# Revit family: MW_Nevada luchtverwarmer
name_source: partatom
category: Mechanical Equipment
units: mm (PartAtom-declared; Revit-internal decimal feet)

## family parameters
Always vertical = Yes
Cut with Voids When Loaded = No
OmniClass Number = 23.75.00.00
OmniClass Title = Climate Control (HVAC)
Part Type = Normal
Room Calculation Point = No
Round Connector Dimension = Use Diameter
Shared = No
Work Plane-Based = No

## types (9) — shared parameters
Manufacturer = Masterwatt B.V.
Materiaal 1 = Coating wit
URL = https://masterwatt.nl
Voltage = 400 V
zero-valued in all types: Default Elevation

## per-type parameters (varying)
| type | Art. No. | Beugel | Breedte | Product type | Watt |
| Nevada 1E 4,5 | 700 100 045 | Nevada_arm : 1E | 530 mm  [stored 1.73885 ft] | Nevada Luchtverwarmer : Nevada 1E 4,5 | 4500 VA |
| Nevada 2E 10,0 | 700 100 100 | Nevada_arm : 2E | 680 mm  [stored 2.23097 ft] | Nevada Luchtverwarmer : Nevada 2E 10,0 | 10000 VA |
| Nevada 1E 6,0 | 700 100 060 | Nevada_arm : 1E | 530 mm  [stored 1.73885 ft] | Nevada Luchtverwarmer : Nevada 1E 4,5 | 6000 VA |
| Nevada 1E 7,5 | 700 100 075 | Nevada_arm : 1E | 530 mm  [stored 1.73885 ft] | Nevada Luchtverwarmer : Nevada 1E 4,5 | 7500 VA |
| Nevada 1E 9,0 | 700 100 090 | Nevada_arm : 1E | 530 mm  [stored 1.73885 ft] | Nevada Luchtverwarmer : Nevada 1E 4,5 | 9000 VA |
| Nevada 2E 12,5 | 700 100 125 | Nevada_arm : 2E | 680 mm  [stored 2.23097 ft] | Nevada Luchtverwarmer : Nevada 2E 10,0 | 12500 VA |
| Nevada 2E 15,0 | 700 100 150 | Nevada_arm : 2E | 680 mm  [stored 2.23097 ft] | Nevada Luchtverwarmer : Nevada 2E 10,0 | 15000 VA |
| Nevada 2E 17,5 | 700 100 175 | Nevada_arm : 2E | 680 mm  [stored 2.23097 ft] | Nevada Luchtverwarmer : Nevada 2E 10,0 | 17500 VA |
| Nevada 2E 20,0 | 700 100 200 | Nevada_arm : 2E | 680 mm  [stored 2.23097 ft] | Nevada Luchtverwarmer : Nevada 2E 10,0 | 20000 VA |

note: column(s) folded — value = type name in every type: Model

note: [stored X ft] marks values corroborated as IEEE doubles in the binary element streams (Revit-internal decimal feet)

## geometry (parser evidence)
native form markers: Sweep x32
no freeform markers — native parametric forms only
